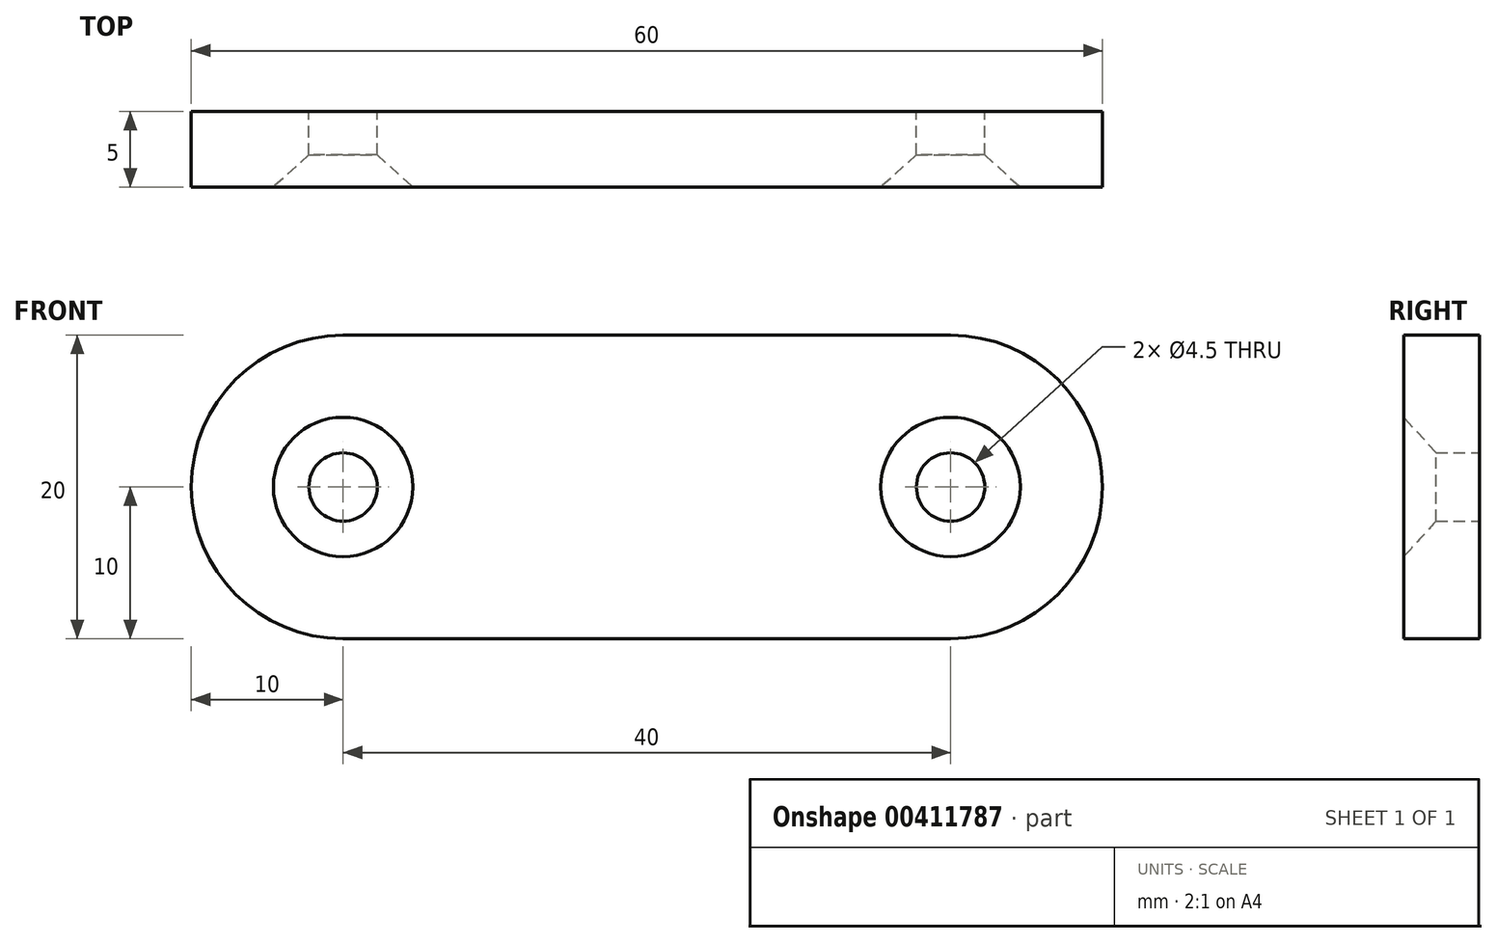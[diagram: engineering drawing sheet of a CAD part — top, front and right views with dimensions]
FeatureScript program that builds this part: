
annotation { "Feature Type Name" : "Feature", "Feature Type Description" : "" }
export const myFeature = defineFeature(function(context is Context, id is Id, definition is map)
    precondition{}
    {
        {
            var Q0;
            Q0=qCreatedBy(makeId("Front.planeOp"),FACE);
            var sketch = newSketch(context, id + "F0", { "sketchPlane" : qUnion([Q0])});
            skArc(sketch, "E0", {"start": v(-20, 10) * mm, "mid": v(-30, 0) * mm, "end": v(-20, -10) * mm});
            skArc(sketch, "E1", {"start": v(20, -10) * mm, "mid": v(30, 0) * mm, "end": v(20, 10) * mm});
            skLineSegment(sketch, "E2", {"start": v(-20, 10) * mm, "end": v(20, 10) * mm});
            skLineSegment(sketch, "E3", {"start": v(-20, -10) * mm, "end": v(20, -10) * mm});
            skCircle(sketch, "E4", {"center": v(-20, 0) * mm, "radius": 2.25 * mm});
            skCircle(sketch, "E5", {"center": v(20, 0) * mm, "radius": 2.25 * mm});
            skSolve(sketch);
        }
        {
            var Q0;
            Q0=qSketchRegion(id+"F0",true);
            extrude(context, id + "F1", {"entities" : qUnion([Q0]), "depth" : 5 * mm});
        }
        {
            var Q0;
            Q0=makeQuery(id+"F1.opExtrude","CAP_EDGE",EDGE,{"disambiguationData":[OSD([sQuery(id+"F0.wireOp",EDGE,"E5")])],"isStart":false});
            var Q1;
            Q1=makeQuery(id+"F1.opExtrude","CAP_EDGE",EDGE,{"disambiguationData":[OSD([sQuery(id+"F0.wireOp",EDGE,"E4")])],"isStart":false});
            chamfer(context, id + "F2", {"entities" : qUnion([Q0, Q1]), "chamferType" : ChamferType.TWO_OFFSETS, "width1" : 2.14 * mm, "oppositeDirection" : false, "width2" : 2.34 * mm, "tangentPropagation" : true});
        }
    });
